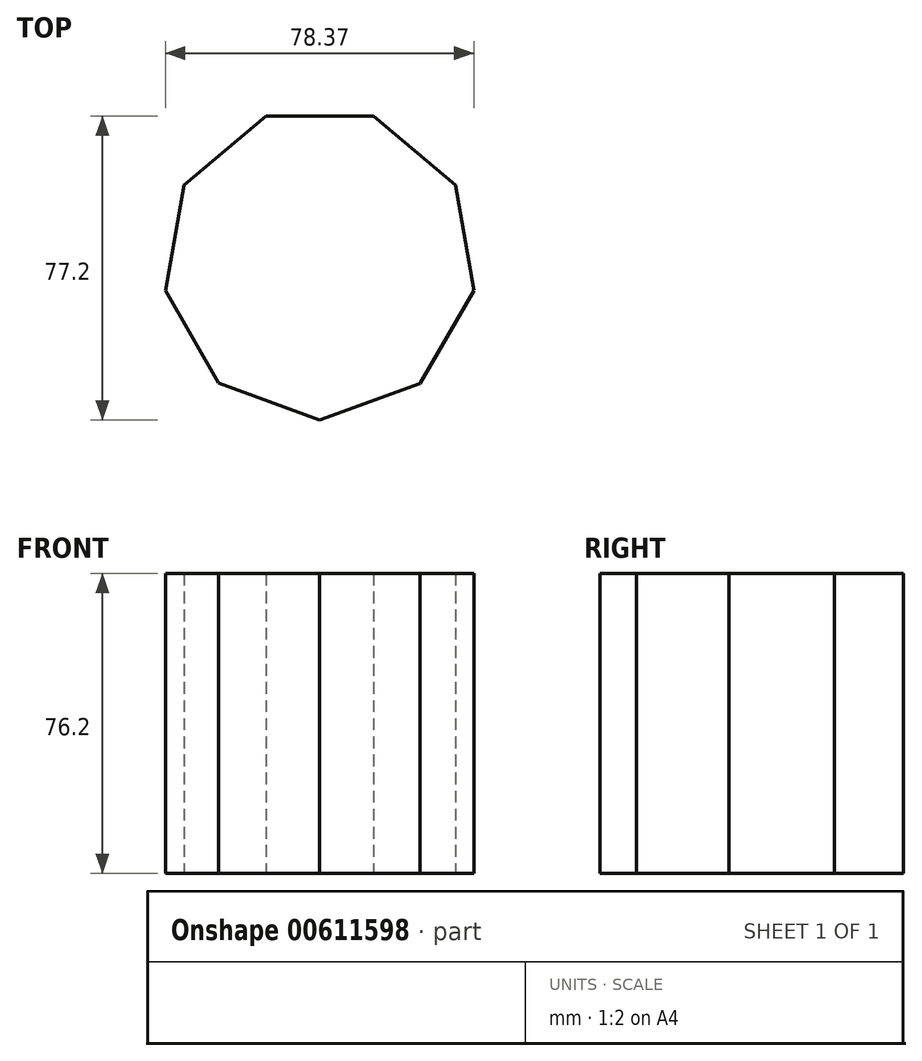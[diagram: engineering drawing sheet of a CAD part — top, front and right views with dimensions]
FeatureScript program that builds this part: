
annotation { "Feature Type Name" : "Feature", "Feature Type Description" : "" }
export const myFeature = defineFeature(function(context is Context, id is Id, definition is map)
    precondition{}
    {
        {
            var Q0;
            Q0=qCreatedBy(makeId("Top.planeOp"),FACE);
            var sketch = newSketch(context, id + "F0", { "sketchPlane" : qUnion([Q0])});
            skCircle(sketch, "E0.cCircle", {"center": v(0, 0) * mm, "radius": 37.4 * mm, "construction": true});
            skLineSegment(sketch, "E0.0", {"start": v(13.66, 37.37) * mm, "end": v(34.49, 19.85) * mm});
            skLineSegment(sketch, "E0.1", {"start": v(34.49, 19.85) * mm, "end": v(39.18, -6.96) * mm});
            skLineSegment(sketch, "E0.2", {"start": v(39.18, -6.96) * mm, "end": v(25.54, -30.51) * mm});
            skLineSegment(sketch, "E0.3", {"start": v(25.54, -30.51) * mm, "end": v(-0.05, -39.8) * mm});
            skLineSegment(sketch, "E0.4", {"start": v(-0.05, -39.8) * mm, "end": v(-25.62, -30.45) * mm});
            skLineSegment(sketch, "E0.5", {"start": v(-25.62, -30.45) * mm, "end": v(-39.2, -6.86) * mm});
            skLineSegment(sketch, "E0.6", {"start": v(-39.2, -6.86) * mm, "end": v(-34.43, 19.94) * mm});
            skLineSegment(sketch, "E0.7", {"start": v(-34.43, 19.94) * mm, "end": v(-13.56, 37.4) * mm});
            skLineSegment(sketch, "E0.8", {"start": v(-13.56, 37.4) * mm, "end": v(13.66, 37.37) * mm});
            skPoint(sketch, "E0.0.midPoint", {"position": v(24.07, 28.61) * mm});
            skSolve(sketch);
        }
        {
            var Q0;
            Q0 = qSketchRegion(id + "F0", true);
            extrude(context, id + "F1", {"entities" : qUnion([Q0]), "depth" : 76.2 * mm, "offsetDistance" : 25.4 * mm});
        }
    });
